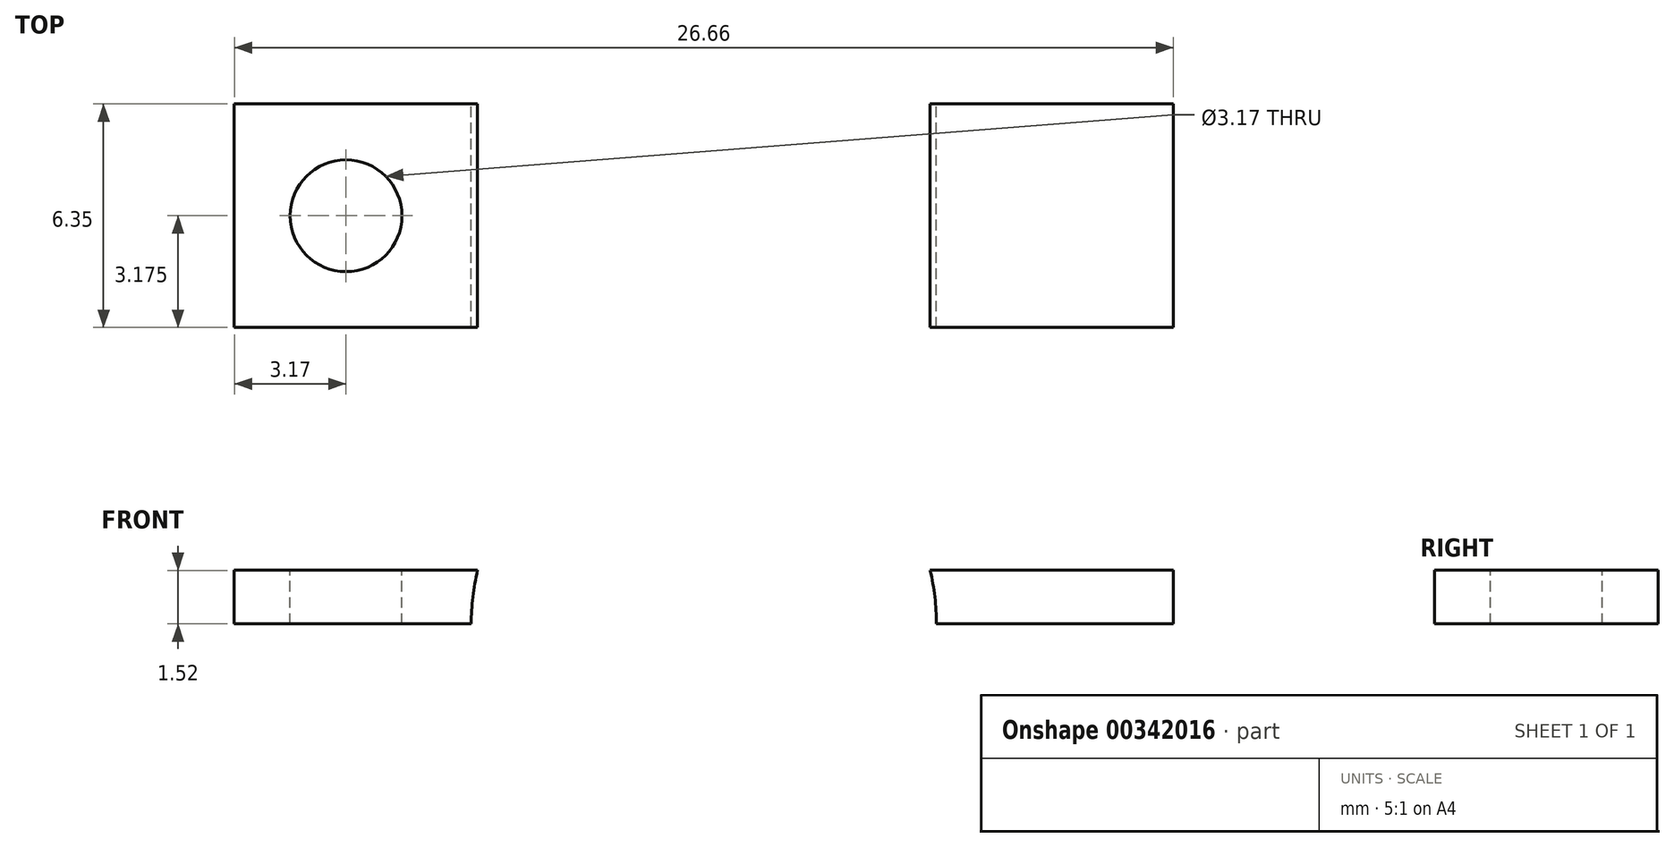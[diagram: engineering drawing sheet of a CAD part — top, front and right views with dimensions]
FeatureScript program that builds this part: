
annotation { "Feature Type Name" : "Feature", "Feature Type Description" : "" }
export const myFeature = defineFeature(function(context is Context, id is Id, definition is map)
    precondition{}
    {
        {
            var Q0;
            Q0=qCreatedBy(makeId("Front.planeOp"),FACE);
            var sketch = newSketch(context, id + "F0", { "sketchPlane" : qUnion([Q0])});
            skLineSegment(sketch, "E0", {"start": v(-5.08, 0) * mm, "end": v(-13.34, 0) * mm});
            skLineSegment(sketch, "E1", {"start": v(-13.34, 0) * mm, "end": v(-13.34, 1.52) * mm});
            skLineSegment(sketch, "E2", {"start": v(-13.34, 1.52) * mm, "end": v(-9.25, 1.52) * mm});
            skArc(sketch, "E3", {"start": v(-5.08, 0) * mm, "mid": v(-3.6, 3.6) * mm, "end": v(0, 5.08) * mm});
            skArc(sketch, "E4", {"start": v(-6.6, 0) * mm, "mid": v(-4.67, 4.67) * mm, "end": v(0, 6.6) * mm});
            skLineSegment(sketch, "E5", {"start": v(-9.25, 1.52) * mm, "end": v(-6.43, 1.52) * mm});
            skArc(sketch, "E6.MirrorCS", {"start": v(5.08, 0) * mm, "mid": v(3.6, 3.6) * mm, "end": v(0, 5.08) * mm});
            skArc(sketch, "E7.MirrorCS", {"start": v(6.6, 0) * mm, "mid": v(4.67, 4.67) * mm, "end": v(0, 6.6) * mm});
            skLineSegment(sketch, "E8.MirrorCS", {"start": v(5.08, 0) * mm, "end": v(13.34, 0) * mm});
            skLineSegment(sketch, "E9.MirrorCS", {"start": v(9.25, 1.52) * mm, "end": v(6.43, 1.52) * mm});
            skLineSegment(sketch, "E10.MirrorCS", {"start": v(13.34, 0) * mm, "end": v(13.34, 1.52) * mm});
            skLineSegment(sketch, "E11.MirrorCS", {"start": v(13.34, 1.52) * mm, "end": v(9.25, 1.52) * mm});
            skSolve(sketch);
        }
        {
            var Q0;
            {var subQ4=sQuery(id+"F0.wireOp",EDGE,"E1");Q0=makeQuery(id+"F0.imprint","IMPRINT",FACE,{"disambiguationData":[TD([[makeQuery(id+"F0.imprint","IMPRINT",EDGE,{"derivedFrom":subQ4}),-1.0]])]});}
            var Q1;
            {var subQ4=sQuery(id+"F0.wireOp",EDGE,"E3");Q1=makeQuery(id+"F0.imprint","IMPRINT",FACE,{"disambiguationData":[TD([[makeQuery(id+"F0.imprint","IMPRINT",EDGE,{"derivedFrom":subQ4}),1.0]])]});}
            var Q2;
            {var subQ0=sQuery(id+"F0.wireOp",EDGE,"E9.MirrorCS");Q2=makeQuery(id+"F0.imprint","IMPRINT",FACE,{"disambiguationData":[TD([[makeQuery(id+"F0.imprint","IMPRINT",EDGE,{"derivedFrom":subQ0}),1.0]])]});}
            extrude(context, id + "F1", {"entities" : qUnion([Q0, Q1, Q2]), "depth" : 6.35 * mm});
        }
        {
            var Q0;
            Q0=makeQuery(id+"F1.opExtrude","SWEPT_FACE",FACE,{"disambiguationData":[OSD([sQuery(id+"F0.wireOp",EDGE,"E2"),sQuery(id+"F0.wireOp",EDGE,"E5")])]});
            var sketch = newSketch(context, id + "F2", { "sketchPlane" : qUnion([Q0])});
            skCircle(sketch, "E12", {"center": v(-10.16, -3.18) * mm, "radius": 1.59 * mm});
            skPoint(sketch, "E12.centerSnap0", {"position": v(-13.34, -3.18) * mm});
            skCircle(sketch, "E13.MirrorC", {"center": v(10.16, -3.18) * mm, "radius": 1.59 * mm});
            skSolve(sketch);
        }
        {
            var Q0;
            Q0=makeQuery(id+"F2.imprint","IMPRINT",FACE,{"disambiguationData":[TD([[makeQuery(id+"F2.imprint","IMPRINT",EDGE,{"derivedFrom":sQuery(id+"F2.wireOp",EDGE,"E13.MirrorC")}),-1.0]])]});
            var Q1;
            Q1=makeQuery(id+"F2.imprint","IMPRINT",FACE,{"disambiguationData":[TD([[makeQuery(id+"F2.imprint","IMPRINT",EDGE,{"derivedFrom":sQuery(id+"F2.wireOp",EDGE,"E12")}),1.0]])]});
            extrude(context, id + "F3", {"entities" : qUnion([Q0, Q1]), "operationType" : NewBodyOperationType.REMOVE, "endBound" : BoundingType.THROUGH_ALL, "oppositeDirection" : true, "depth" : 25.4 * mm});
        }
    });
